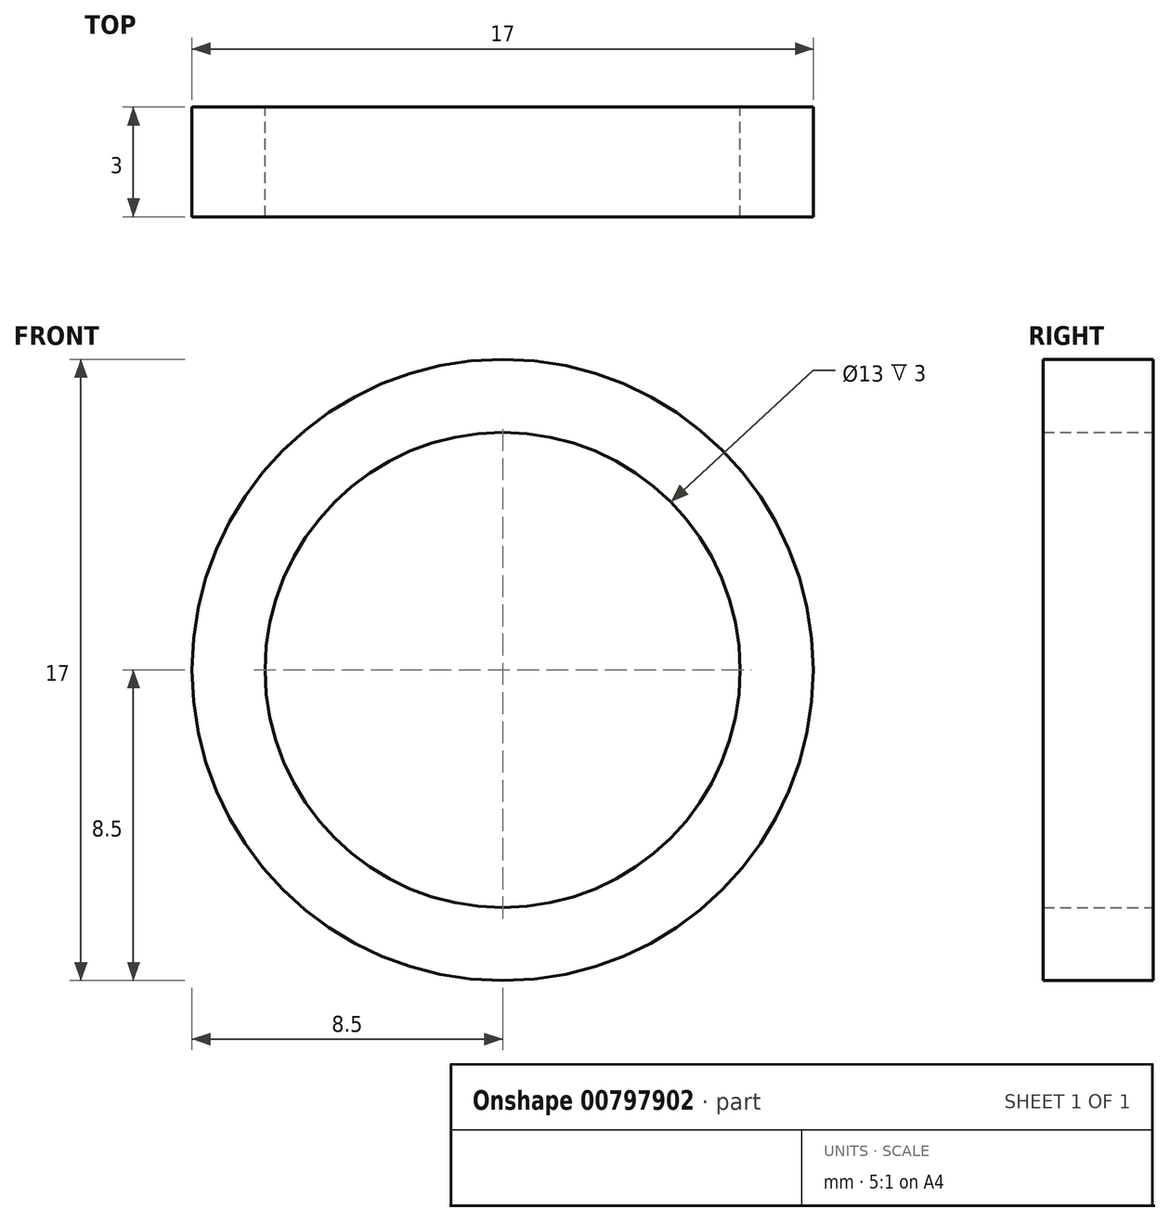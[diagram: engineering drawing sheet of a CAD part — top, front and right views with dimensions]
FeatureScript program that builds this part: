
annotation { "Feature Type Name" : "Feature", "Feature Type Description" : "" }
export const myFeature = defineFeature(function(context is Context, id is Id, definition is map)
    precondition{}
    {
        {
            var Q0;
            Q0=qCreatedBy(makeId("Front.planeOp"),FACE);
            var sketch = newSketch(context, id + "F0", { "sketchPlane" : qUnion([Q0])});
            skCircle(sketch, "E0", {"center": v(0, 0) * mm, "radius": 6.5 * mm});
            skCircle(sketch, "E1", {"center": v(0, 0) * mm, "radius": 8.5 * mm});
            skSolve(sketch);
        }
        {
            var Q0;
            Q0 = qSketchRegion(id + "F0", true);
            extrude(context, id + "F1", {"entities" : qUnion([Q0]), "depth" : 3 * mm, "offsetDistance" : 25 * mm});
        }
    });
